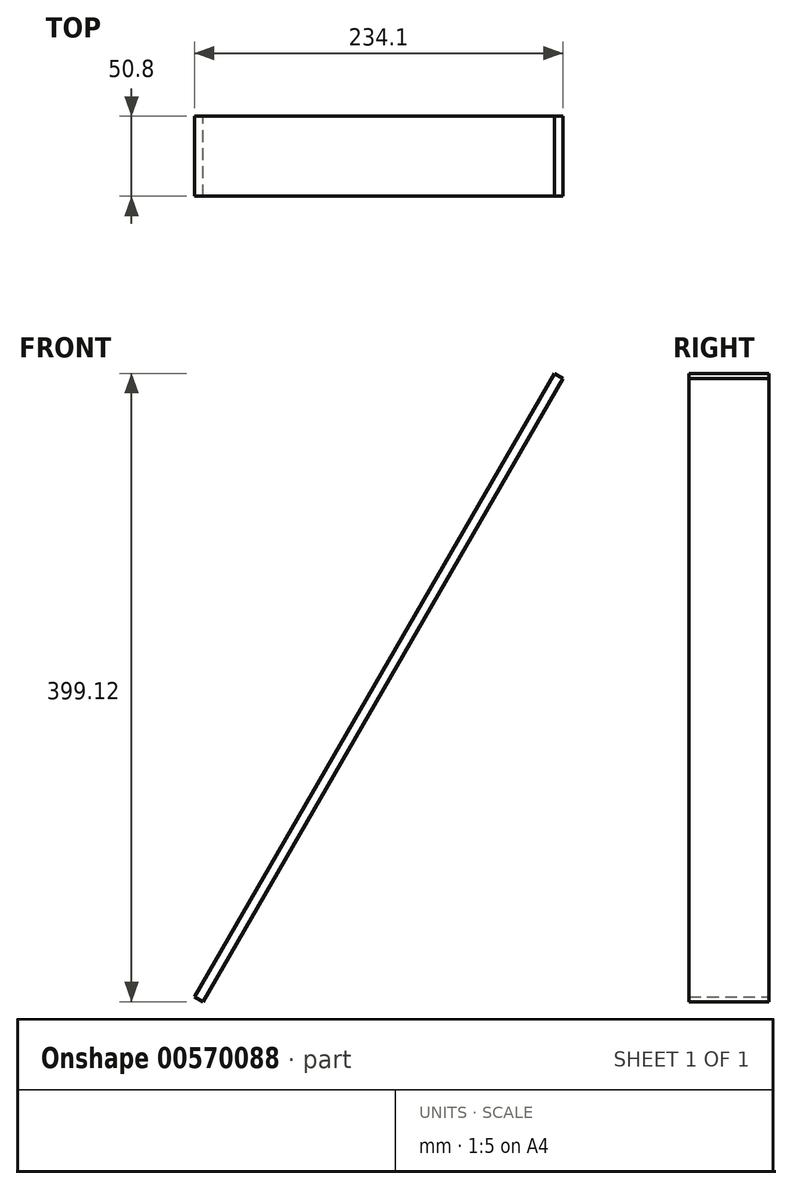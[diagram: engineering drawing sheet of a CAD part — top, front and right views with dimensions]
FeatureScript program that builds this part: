
annotation { "Feature Type Name" : "Feature", "Feature Type Description" : "" }
export const myFeature = defineFeature(function(context is Context, id is Id, definition is map)
    precondition{}
    {
        {
            var Q0;
            Q0=qCreatedBy(makeId("Right.planeOp"),FACE);
            var sketch = newSketch(context, id + "F0", { "sketchPlane" : qUnion([Q0])});
            skLineSegment(sketch, "E0", {"start": v(0, 0) * mm, "end": v(50.8, 0) * mm});
            skLineSegment(sketch, "E1", {"start": v(50.8, 0) * mm, "end": v(50.8, 457.2) * mm});
            skLineSegment(sketch, "E2", {"start": v(50.8, 457.2) * mm, "end": v(0, 457.2) * mm});
            skLineSegment(sketch, "E3", {"start": v(0, 0) * mm, "end": v(0, 457.2) * mm});
            skSolve(sketch);
        }
        {
            var Q0;
            Q0=makeQuery(id+"F0.imprint","IMPRINT",FACE,{"disambiguationData":[TD([[makeQuery(id+"F0.imprint","IMPRINT",EDGE,{"derivedFrom":sQuery(id+"F0.wireOp",EDGE,"E0")}),1.0]])]});
            extrude(context, id + "F1", {"entities" : qUnion([Q0]), "depth" : 6.35 * mm, "offsetDistance" : 25.4 * mm});
        }
        {
            var Q0;
            Q0=makeQuery(id+"F1.opExtrude","SWEPT_BODY",BODY,{"disambiguationData":[OSD([sQuery(id+"F0.wireOp",EDGE,"E0"),sQuery(id+"F0.wireOp",EDGE,"E1"),sQuery(id+"F0.wireOp",EDGE,"E2"),sQuery(id+"F0.wireOp",EDGE,"E3")])]});
            var Q1;
            Q1=makeQuery(id+"F1.opExtrude","CAP_EDGE",EDGE,{"disambiguationData":[OSD([sQuery(id+"F0.wireOp",EDGE,"E0")])],"isStart":true});
            transform(context, id + "F2", {"entities" : qUnion([Q0]), "transformType" : TransformType.ROTATION, "transformAxis" : qUnion([Q1]), "angle" : 30 * degree, "makeCopy" : false});
        }
    });
